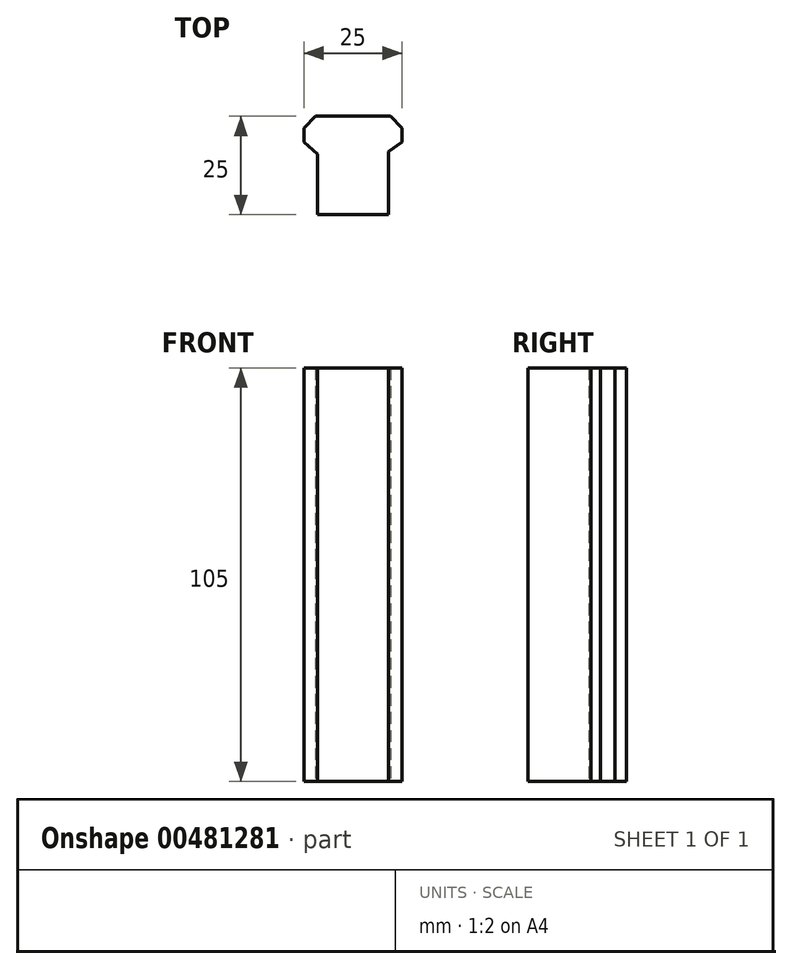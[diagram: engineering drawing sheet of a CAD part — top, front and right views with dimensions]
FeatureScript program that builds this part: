
annotation { "Feature Type Name" : "Feature", "Feature Type Description" : "" }
export const myFeature = defineFeature(function(context is Context, id is Id, definition is map)
    precondition{}
    {
        {
            var Q0;
            Q0=qCreatedBy(makeId("Top.planeOp"),FACE);
            var sketch = newSketch(context, id + "F0", { "sketchPlane" : qUnion([Q0])});
            skLineSegment(sketch, "E0", {"start": v(12.5, 0.1) * mm, "end": v(12.5, -9) * mm});
            skLineSegment(sketch, "E1.MirrorCS", {"start": v(-12.5, -3) * mm, "end": v(-12.5, -6.6) * mm});
            skPoint(sketch, "E2", {"position": v(0, -9) * mm});
            skPoint(sketch, "E3", {"position": v(3.68, -20.16) * mm});
            skLineSegment(sketch, "E4", {"start": v(0, -9) * mm, "end": v(0, -25) * mm, "construction": true});
            skLineSegment(sketch, "E5", {"start": v(-9.05, -25) * mm, "end": v(9.05, -25) * mm});
            skLineSegment(sketch, "E6", {"start": v(9.05, -25) * mm, "end": v(9.05, -9) * mm});
            skLineSegment(sketch, "E7", {"start": v(-9.05, -25) * mm, "end": v(-9.05, -9.6) * mm});
            skLineSegment(sketch, "E8", {"start": v(-9.5, 0) * mm, "end": v(9.5, 0) * mm});
            skLineSegment(sketch, "E9", {"start": v(0, 0) * mm, "end": v(0, -3) * mm, "construction": true});
            skPoint(sketch, "E10", {"position": v(12.5, -3) * mm});
            skPoint(sketch, "E11", {"position": v(-12.5, -3) * mm});
            skLineSegment(sketch, "E12", {"start": v(-12.5, -3) * mm, "end": v(-9.5, 0) * mm});
            skLineSegment(sketch, "E13", {"start": v(9.5, 0) * mm, "end": v(12.5, -3) * mm});
            skPoint(sketch, "E14", {"position": v(12.5, -6.6) * mm});
            skPoint(sketch, "E15", {"position": v(-12.5, -6.6) * mm});
            skLineSegment(sketch, "E16", {"start": v(-12.5, -6.6) * mm, "end": v(-9.05, -9.6) * mm});
            skLineSegment(sketch, "E17", {"start": v(12.5, -6.6) * mm, "end": v(9.05, -9) * mm});
            skPoint(sketch, "E18.end.orphan", {"position": v(-12.5, -9.6) * mm});
            skSolve(sketch);
        }
        {
            var Q0;
            Q0=makeQuery(id+"F0.imprint","IMPRINT",FACE,{"disambiguationData":[TD([[makeQuery(id+"F0.imprint","IMPRINT",EDGE,{"derivedFrom":sQuery(id+"F0.wireOp",EDGE,"E1.MirrorCS")}),1.0]])]});
            extrude(context, id + "F1", {"entities" : qUnion([Q0]), "depth" : 105 * mm});
        }
    });
